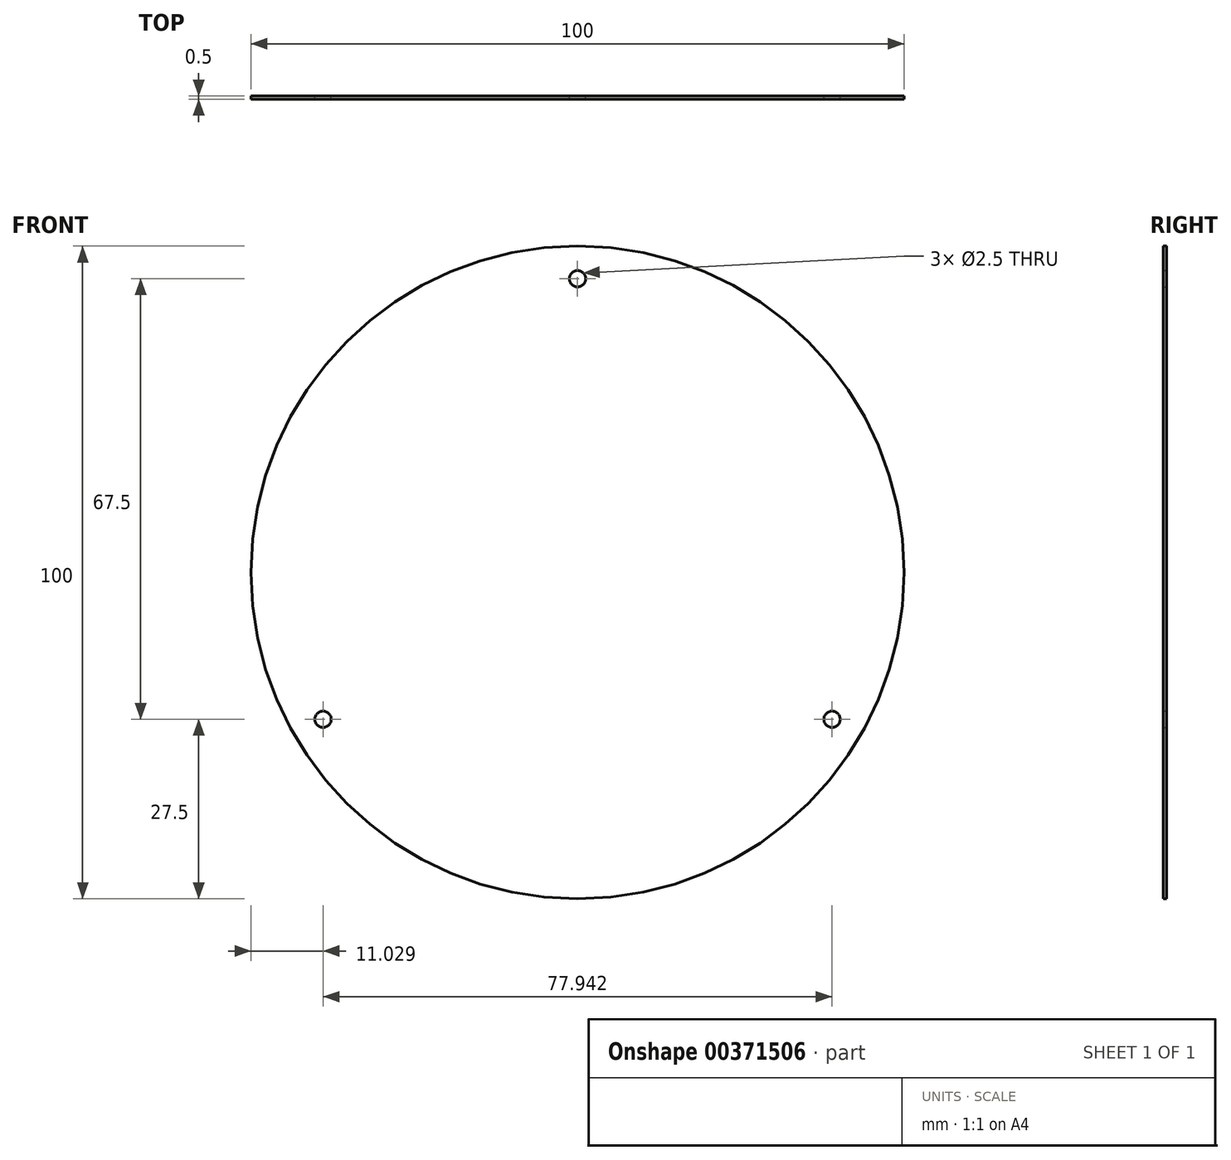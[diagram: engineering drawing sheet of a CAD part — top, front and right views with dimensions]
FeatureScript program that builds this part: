
annotation { "Feature Type Name" : "Feature", "Feature Type Description" : "" }
export const myFeature = defineFeature(function(context is Context, id is Id, definition is map)
    precondition{}
    {
        {
            var Q0;
            Q0=qCreatedBy(makeId("Front.planeOp"),FACE);
            var sketch = newSketch(context, id + "F0", { "sketchPlane" : qUnion([Q0])});
            skCircle(sketch, "E0", {"center": v(0, 0) * mm, "radius": 50 * mm});
            skCircle(sketch, "E1", {"center": v(0, 0) * mm, "radius": 45 * mm, "construction": true});
            skLineSegment(sketch, "E2", {"start": v(0, 64.91) * mm, "end": v(0, -67.99) * mm, "construction": true});
            skCircle(sketch, "E3", {"center": v(0, 45) * mm, "radius": 1.25 * mm});
            skLineSegment(sketch, "E4", {"start": v(-61.6, 0) * mm, "end": v(62.53, 0) * mm, "construction": true});
            skCircle(sketch, "E5.1.0", {"center": v(-38.97, -22.5) * mm, "radius": 1.25 * mm});
            skCircle(sketch, "E5.2.0", {"center": v(38.97, -22.5) * mm, "radius": 1.25 * mm});
            skLineSegment(sketch, "E6", {"start": v(-38.97, -22.5) * mm, "end": v(0, 0) * mm, "construction": true});
            skLineSegment(sketch, "E7", {"start": v(38.97, -22.5) * mm, "end": v(0, 0) * mm, "construction": true});
            skSolve(sketch);
        }
        {
            var Q0;
            Q0=makeQuery(id+"F0.imprint","IMPRINT",FACE,{"disambiguationData":[TD([[makeQuery(id+"F0.imprint","IMPRINT",EDGE,{"derivedFrom":sQuery(id+"F0.wireOp",EDGE,"E0")}),1.0]])]});
            extrude(context, id + "F1", {"entities" : qUnion([Q0]), "depth" : .5 * mm, "offsetDistance" : 25 * mm});
        }
    });
